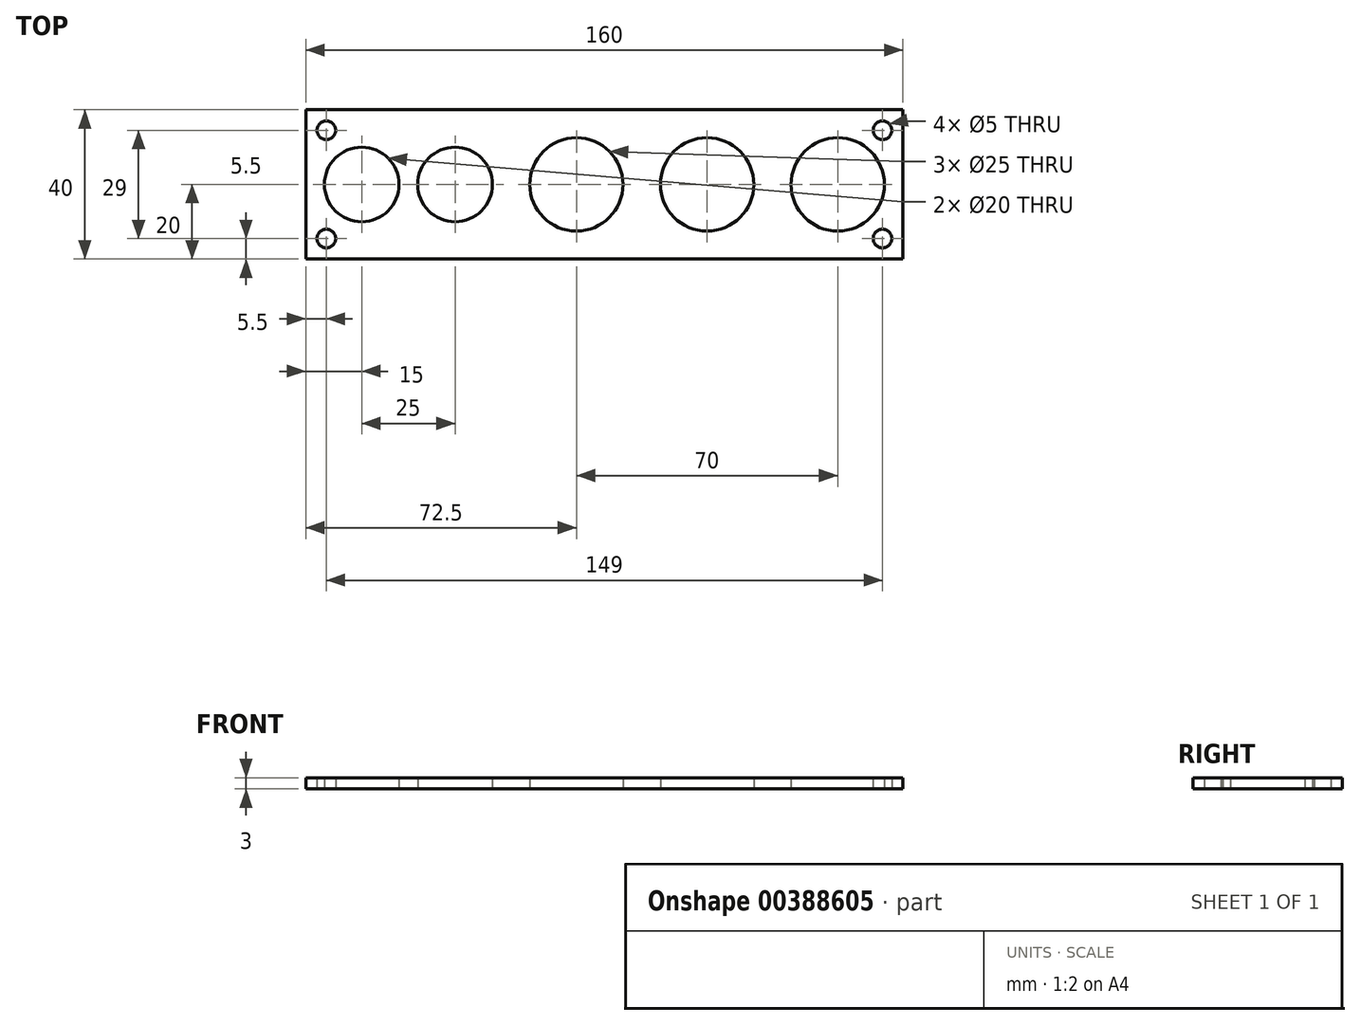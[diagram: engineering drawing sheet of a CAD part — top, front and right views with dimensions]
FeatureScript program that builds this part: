
annotation { "Feature Type Name" : "Feature", "Feature Type Description" : "" }
export const myFeature = defineFeature(function(context is Context, id is Id, definition is map)
    precondition{}
    {
        {
            var Q0;
            Q0=qCreatedBy(makeId("Top.planeOp"),FACE);
            var sketch = newSketch(context, id + "F0", { "sketchPlane" : qUnion([Q0])});
            skLineSegment(sketch, "E0.bottom", {"start": v(-80, 20) * mm, "end": v(80, 20) * mm});
            skLineSegment(sketch, "E0.top", {"start": v(-80, -20) * mm, "end": v(80, -20) * mm});
            skLineSegment(sketch, "E0.left", {"start": v(-80, 20) * mm, "end": v(-80, -20) * mm});
            skLineSegment(sketch, "E0.right", {"start": v(80, 20) * mm, "end": v(80, -20) * mm});
            skCircle(sketch, "E1", {"center": v(-65, 0) * mm, "radius": 10 * mm});
            skCircle(sketch, "E2.1.0.0", {"center": v(-40, 0) * mm, "radius": 10 * mm});
            skCircle(sketch, "E3", {"center": v(62.5, 0) * mm, "radius": 12.5 * mm});
            skCircle(sketch, "E4.1.0.0", {"center": v(27.5, 0) * mm, "radius": 12.5 * mm});
            skCircle(sketch, "E4.2.0.0", {"center": v(-7.5, 0) * mm, "radius": 12.5 * mm});
            skCircle(sketch, "E5", {"center": v(-74.5, 14.5) * mm, "radius": 2.5 * mm});
            skCircle(sketch, "E6", {"center": v(74.5, 14.5) * mm, "radius": 2.5 * mm});
            skCircle(sketch, "E7", {"center": v(-74.5, -14.5) * mm, "radius": 2.5 * mm});
            skCircle(sketch, "E8", {"center": v(74.5, -14.5) * mm, "radius": 2.5 * mm});
            skSolve(sketch);
        }
        {
            var Q0;
            Q0 = qSketchRegion(id + "F0", true);
            extrude(context, id + "F1", {"entities" : qUnion([Q0]), "depth" : 3 * mm});
        }
    });
